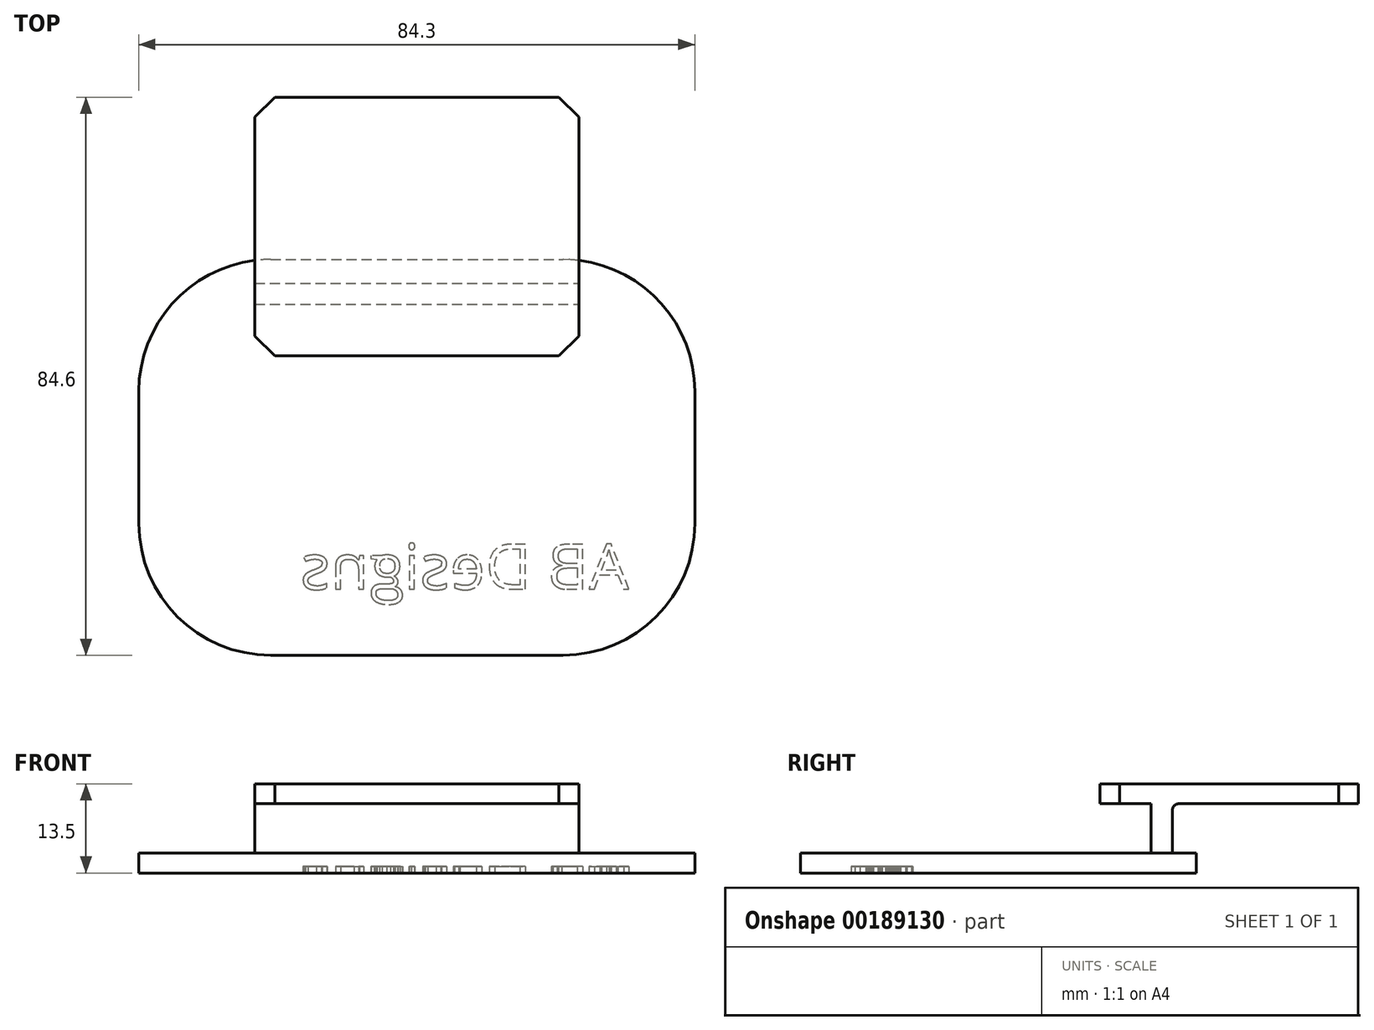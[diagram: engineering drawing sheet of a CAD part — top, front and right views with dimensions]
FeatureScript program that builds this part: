
annotation { "Feature Type Name" : "Feature", "Feature Type Description" : "" }
export const myFeature = defineFeature(function(context is Context, id is Id, definition is map)
    precondition{}
    {
        {
            var Q0;
            Q0=qCreatedBy(makeId("Top.planeOp"),FACE);
            var sketch = newSketch(context, id + "F0", { "sketchPlane" : qUnion([Q0])});
            skLineSegment(sketch, "E0.bottom", {"start": v(-22.15, 42.15) * mm, "end": v(22.15, 42.15) * mm});
            skLineSegment(sketch, "E0.top", {"start": v(-22.15, -17.85) * mm, "end": v(22.15, -17.85) * mm});
            skLineSegment(sketch, "E0.left", {"start": v(-42.15, 22.15) * mm, "end": v(-42.15, 2.15) * mm});
            skLineSegment(sketch, "E0.right", {"start": v(42.15, 22.15) * mm, "end": v(42.15, 2.15) * mm});
            skPoint(sketch, "E1.visualSharp", {"position": v(-42.15, 42.15) * mm});
            skArc(sketch, "E1.filletArc", {"start": v(-22.15, 42.15) * mm, "mid": v(-36.3, 36.3) * mm, "end": v(-42.15, 22.15) * mm});
            skPoint(sketch, "E2.visualSharp", {"position": v(42.15, 42.15) * mm});
            skArc(sketch, "E2.filletArc", {"start": v(42.15, 22.15) * mm, "mid": v(36.3, 36.3) * mm, "end": v(22.15, 42.15) * mm});
            skPoint(sketch, "E3.visualSharp", {"position": v(42.15, -17.85) * mm});
            skArc(sketch, "E3.filletArc", {"start": v(22.15, -17.85) * mm, "mid": v(36.3, -12) * mm, "end": v(42.15, 2.15) * mm});
            skPoint(sketch, "E4.visualSharp", {"position": v(-42.15, -17.85) * mm});
            skArc(sketch, "E4.filletArc", {"start": v(-42.15, 2.15) * mm, "mid": v(-36.3, -12) * mm, "end": v(-22.15, -17.85) * mm});
            skSolve(sketch);
        }
        {
            var Q0;
            Q0 = qSketchRegion(id + "F0", true);
            extrude(context, id + "F1", {"entities" : qUnion([Q0]), "depth" : 3 * mm});
        }
        {
            var Q0;
            Q0=qCreatedBy(makeId("Top.planeOp"),FACE);
            var sketch = newSketch(context, id + "F2", { "sketchPlane" : qUnion([Q0])});
            skLineSegment(sketch, "E5.bottom", {"start": v(-24.55, 38.55) * mm, "end": v(24.55, 38.55) * mm});
            skLineSegment(sketch, "E5.top", {"start": v(-24.55, 35.35) * mm, "end": v(24.55, 35.35) * mm});
            skLineSegment(sketch, "E5.left", {"start": v(-24.55, 38.55) * mm, "end": v(-24.55, 35.35) * mm});
            skLineSegment(sketch, "E5.right", {"start": v(24.55, 38.55) * mm, "end": v(24.55, 35.35) * mm});
            skSolve(sketch);
        }
        {
            var Q0;
            Q0 = qSketchRegion(id + "F2", true);
            extrude(context, id + "F3", {"entities" : qUnion([Q0]), "operationType" : NewBodyOperationType.ADD, "depth" : 13.5 * mm});
        }
        {
            var Q0;
            Q0=qCreatedBy(makeId("Top.planeOp"),FACE);
            cPlane(context, id + "F4", {"entities" : qUnion([Q0]), "cplaneType" : CPlaneType.OFFSET, "offset" : 13.5 * mm, "width" : 150 * mm, "height" : 150 * mm});
        }
        {
            var Q0;
            Q0=qCreatedBy(id+"F4.planeOp",FACE);
            var sketch = newSketch(context, id + "F5", { "sketchPlane" : qUnion([Q0])});
            skLineSegment(sketch, "E6.bottom", {"start": v(-24.55, 66.75) * mm, "end": v(24.55, 66.75) * mm});
            skLineSegment(sketch, "E6.top", {"start": v(-24.55, 27.55) * mm, "end": v(24.55, 27.55) * mm});
            skLineSegment(sketch, "E6.left", {"start": v(-24.55, 66.75) * mm, "end": v(-24.55, 27.55) * mm});
            skLineSegment(sketch, "E6.right", {"start": v(24.55, 66.75) * mm, "end": v(24.55, 27.55) * mm});
            skSolve(sketch);
        }
        {
            var Q0;
            Q0 = qSketchRegion(id + "F5", true);
            extrude(context, id + "F6", {"entities" : qUnion([Q0]), "operationType" : NewBodyOperationType.ADD, "oppositeDirection" : true, "depth" : 3 * mm});
        }
        {
            var Q0;
            Q0=makeQuery(id+"F6.opExtrude","SWEPT_EDGE",EDGE,{"disambiguationData":[OSD([sQuery(id+"F5.wireOp",EDGE,"E6.bottom"),sQuery(id+"F5.wireOp",EDGE,"E6.right")])]});
            chamfer(context, id + "F7", {"entities" : qUnion([Q0]), "width" : 3 * mm, "tangentPropagation" : true});
        }
        {
            var Q0;
            Q0=makeQuery(id+"F6.opExtrude","SWEPT_EDGE",EDGE,{"disambiguationData":[OSD([sQuery(id+"F5.wireOp",EDGE,"E6.bottom"),sQuery(id+"F5.wireOp",EDGE,"E6.left")])]});
            chamfer(context, id + "F8", {"entities" : qUnion([Q0]), "width" : 3 * mm, "tangentPropagation" : true});
        }
        {
            var Q0;
            Q0=makeQuery(id+"F6.opExtrude","SWEPT_EDGE",EDGE,{"disambiguationData":[OSD([sQuery(id+"F5.wireOp",EDGE,"E6.top"),sQuery(id+"F5.wireOp",EDGE,"E6.left")])]});
            chamfer(context, id + "F9", {"entities" : qUnion([Q0]), "width" : 3 * mm, "tangentPropagation" : true});
        }
        {
            var Q0;
            Q0=makeQuery(id+"F6.opExtrude","SWEPT_EDGE",EDGE,{"disambiguationData":[OSD([sQuery(id+"F5.wireOp",EDGE,"E6.top"),sQuery(id+"F5.wireOp",EDGE,"E6.right")])]});
            chamfer(context, id + "F10", {"entities" : qUnion([Q0]), "width" : 3 * mm, "tangentPropagation" : true});
        }
        {
            var Q0;
            Q0=makeQuery(id+"F6.boolean.opBoolean","INTERSECT",EDGE,{"derivedFrom":[makeQuery(id+"F3.opExtrude","SWEPT_FACE",FACE,{"disambiguationData":[OSD([sQuery(id+"F2.wireOp",EDGE,"E5.bottom")])]}),makeQuery(id+"F6.opExtrude","CAP_FACE",FACE,{"disambiguationData":[OSD([sQuery(id+"F5.wireOp",EDGE,"E6.bottom"),sQuery(id+"F5.wireOp",EDGE,"E6.top"),sQuery(id+"F5.wireOp",EDGE,"E6.left"),sQuery(id+"F5.wireOp",EDGE,"E6.right")])],"isStart":false})]});
            fillet(context, id + "F11", {"entities" : qUnion([Q0]), "radius" : 1 * mm, "tangentPropagation" : true, "allowEdgeOverflow" : false});
        }
        {
            var Q0;
            Q0=makeQuery(id+"F1.opExtrude","CAP_FACE",FACE,{"disambiguationData":[OSD([sQuery(id+"F0.wireOp",EDGE,"E0.bottom"),sQuery(id+"F0.wireOp",EDGE,"E0.top"),sQuery(id+"F0.wireOp",EDGE,"E0.left"),sQuery(id+"F0.wireOp",EDGE,"E0.right"),sQuery(id+"F0.wireOp",EDGE,"E1.filletArc"),sQuery(id+"F0.wireOp",EDGE,"E2.filletArc"),sQuery(id+"F0.wireOp",EDGE,"E3.filletArc"),sQuery(id+"F0.wireOp",EDGE,"E4.filletArc")])],"isStart":true});
            cPlane(context, id + "F12", {"entities" : qUnion([Q0]), "cplaneType" : CPlaneType.OFFSET, "offset" : 0 * mm, "width" : 150 * mm, "height" : 150 * mm});
        }
        {
            var Q0;
            Q0=qCreatedBy(id+"F12.planeOp",FACE);
            var sketch = newSketch(context, id + "F13", { "sketchPlane" : qUnion([Q0])});
            skText(sketch, "E7", { "text": "AB Designs", "fontName": "OpenSans-Regular.ttf"});
            const initialGuessF13  = {"E7": [0.03215, 0.00785, -1, 0, 0.0069]};
            skSetInitialGuess(sketch, initialGuessF13);
            skSolve(sketch);
        }
        {
            var Q0;
            Q0 = qSketchRegion(id + "F13", true);
            extrude(context, id + "F14", {"entities" : qUnion([Q0]), "operationType" : NewBodyOperationType.REMOVE, "oppositeDirection" : true, "depth" : 1 * mm});
        }
    });
